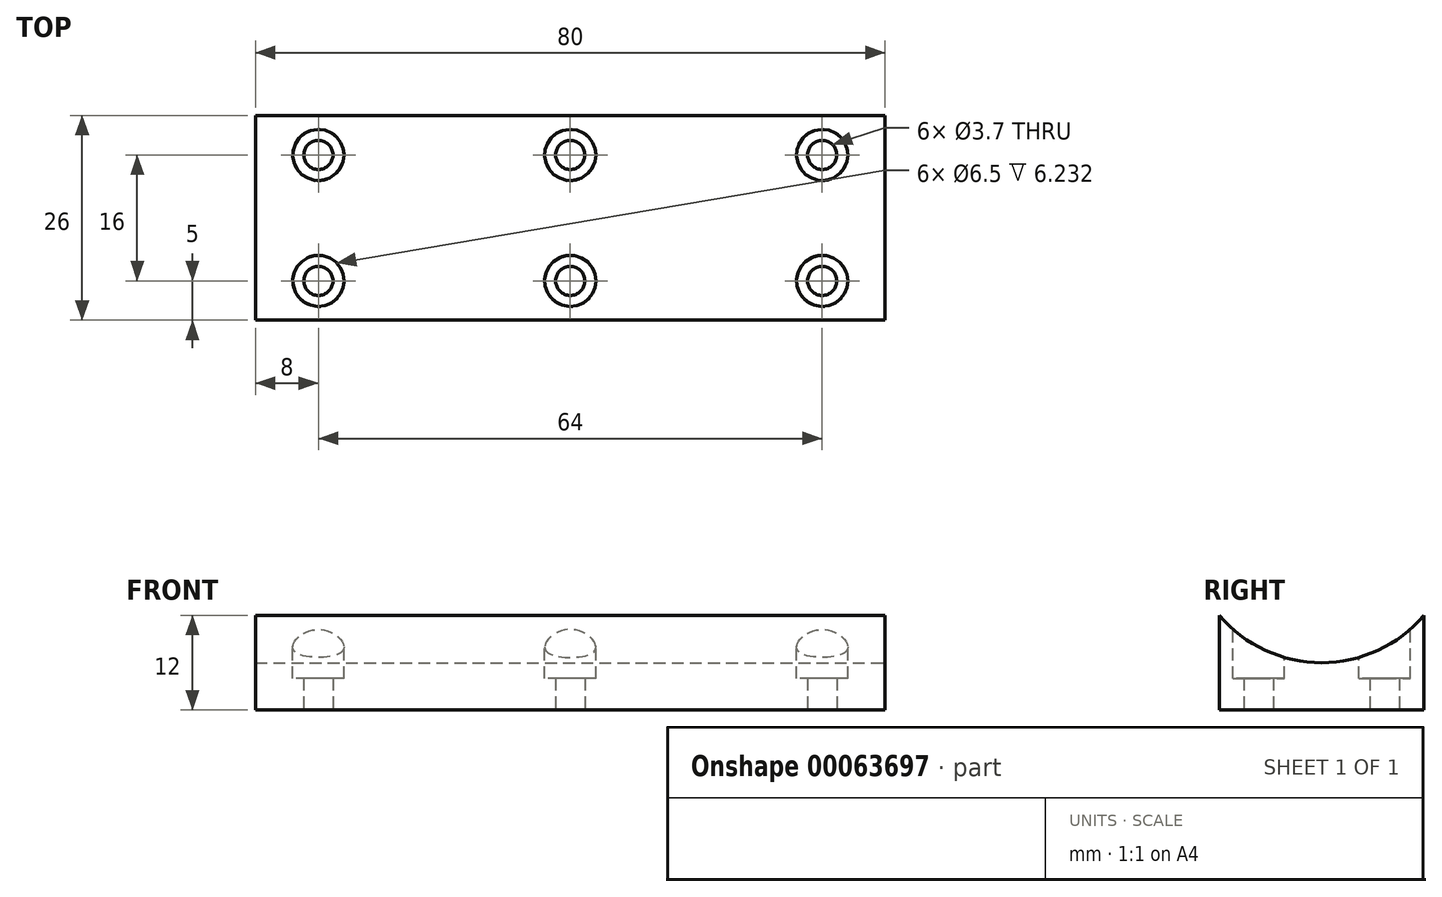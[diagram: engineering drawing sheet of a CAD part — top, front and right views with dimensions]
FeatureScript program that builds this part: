
annotation { "Feature Type Name" : "Feature", "Feature Type Description" : "" }
export const myFeature = defineFeature(function(context is Context, id is Id, definition is map)
    precondition{}
    {
        {
            var Q0;
            Q0=qCreatedBy(makeId("Top.planeOp"),FACE);
            var sketch = newSketch(context, id + "F0", { "sketchPlane" : qUnion([Q0])});
            skLineSegment(sketch, "E0.rect.bottom", {"start": v(-40, -13) * mm, "end": v(40, -13) * mm});
            skLineSegment(sketch, "E0.rect.top", {"start": v(-40, 13) * mm, "end": v(40, 13) * mm});
            skLineSegment(sketch, "E0.rect.left", {"start": v(-40, -13) * mm, "end": v(-40, 13) * mm});
            skLineSegment(sketch, "E0.rect.right", {"start": v(40, -13) * mm, "end": v(40, 13) * mm});
            skPoint(sketch, "E0.rect.middle", {"position": v(0, 0) * mm});
            skCircle(sketch, "E1", {"center": v(0, 8) * mm, "radius": 1.85 * mm});
            skCircle(sketch, "E2.2.0", {"center": v(0, -8) * mm, "radius": 1.85 * mm});
            skPoint(sketch, "E3.1.0.2", {"position": v(32, 0) * mm});
            skCircle(sketch, "E3.1.0.3", {"center": v(32, 8) * mm, "radius": 1.85 * mm});
            skPoint(sketch, "E3.1.0.5", {"position": v(32, 0) * mm});
            skCircle(sketch, "E3.1.0.6", {"center": v(32, -8) * mm, "radius": 1.85 * mm});
            skCircle(sketch, "E4.1.0.0", {"center": v(-32, 8) * mm, "radius": 1.85 * mm});
            skCircle(sketch, "E4.1.0.1", {"center": v(-32, -8) * mm, "radius": 1.85 * mm});
            skLineSegment(sketch, "E4.direction1", {"start": v(0, 8) * mm, "end": v(-32, 8) * mm, "construction": true});
            skSolve(sketch);
        }
        {
            var Q0;
            Q0=makeQuery(id+"F0.imprint","IMPRINT",FACE,{"disambiguationData":[TD([[makeQuery(id+"F0.imprint","IMPRINT",EDGE,{"derivedFrom":sQuery(id+"F0.wireOp",EDGE,"E0.rect.bottom")}),1.0]])]});
            extrude(context, id + "F1", {"entities" : qUnion([Q0]), "depth" : 25 * mm});
        }
        {
            var Q0;
            Q0=makeQuery(id+"F1.opExtrude","SWEPT_FACE",FACE,{"disambiguationData":[OSD([sQuery(id+"F0.wireOp",EDGE,"E0.rect.right")])]});
            var sketch = newSketch(context, id + "F2", { "sketchPlane" : qUnion([Q0])});
            skLineSegment(sketch, "E5", {"start": v(-13, 0) * mm, "end": v(-13, 12) * mm, "construction": true});
            skLineSegment(sketch, "E6", {"start": v(0, 0) * mm, "end": v(0, 6) * mm, "construction": true});
            skPoint(sketch, "E6.endSnap0", {"position": v(0, 0) * mm});
            skArc(sketch, "E7", {"start": v(-13, 12) * mm, "mid": v(0, 6) * mm, "end": v(13, 12) * mm});
            skSolve(sketch);
        }
        {
            var Q0;
            Q0=makeQuery(id+"F1.opExtrude","CAP_FACE",FACE,{"disambiguationData":[OSD([sQuery(id+"F0.wireOp",EDGE,"E0.rect.bottom"),sQuery(id+"F0.wireOp",EDGE,"E0.rect.top"),sQuery(id+"F0.wireOp",EDGE,"E0.rect.left"),sQuery(id+"F0.wireOp",EDGE,"E0.rect.right"),sQuery(id+"F0.wireOp",EDGE,"E1"),sQuery(id+"F0.wireOp",EDGE,"E2.2.0"),sQuery(id+"F0.wireOp",EDGE,"E3.1.0.3"),sQuery(id+"F0.wireOp",EDGE,"E3.1.0.6"),sQuery(id+"F0.wireOp",EDGE,"E4.1.0.0"),sQuery(id+"F0.wireOp",EDGE,"E4.1.0.1")])],"isStart":false});
            var sketch = newSketch(context, id + "F3", { "sketchPlane" : qUnion([Q0])});
            skCircle(sketch, "E8", {"center": v(-32, 8) * mm, "radius": 3.25 * mm});
            skCircle(sketch, "E9", {"center": v(-32, -8) * mm, "radius": 3.25 * mm});
            skCircle(sketch, "E10.1.0.0", {"center": v(0, 8) * mm, "radius": 3.25 * mm});
            skCircle(sketch, "E10.1.0.1", {"center": v(0, -8) * mm, "radius": 3.25 * mm});
            skCircle(sketch, "E10.2.0.0", {"center": v(32, 8) * mm, "radius": 3.25 * mm});
            skCircle(sketch, "E10.2.0.1", {"center": v(32, -8) * mm, "radius": 3.25 * mm});
            skLineSegment(sketch, "E10.direction1", {"start": v(-32, 8) * mm, "end": v(0, 8) * mm, "construction": true});
            skSolve(sketch);
        }
        {
            var Q0;
            Q0=makeQuery(id+"F3.imprint","IMPRINT",FACE,{"disambiguationData":[TD([[makeQuery(id+"F3.imprint","IMPRINT",EDGE,{"derivedFrom":sQuery(id+"F3.wireOp",EDGE,"E9")}),1.0]])]});
            var Q1;
            Q1=makeQuery(id+"F3.imprint","IMPRINT",FACE,{"disambiguationData":[TD([[makeQuery(id+"F3.imprint","IMPRINT",EDGE,{"derivedFrom":sQuery(id+"F3.wireOp",EDGE,"E8")}),1.0]])]});
            var Q2;
            Q2=makeQuery(id+"F3.imprint","IMPRINT",FACE,{"disambiguationData":[TD([[makeQuery(id+"F3.imprint","IMPRINT",EDGE,{"derivedFrom":sQuery(id+"F3.wireOp",EDGE,"E10.1.0.0")}),1.0]])]});
            var Q3;
            Q3=makeQuery(id+"F3.imprint","IMPRINT",FACE,{"disambiguationData":[TD([[makeQuery(id+"F3.imprint","IMPRINT",EDGE,{"derivedFrom":sQuery(id+"F3.wireOp",EDGE,"E10.1.0.1")}),1.0]])]});
            var Q4;
            Q4=makeQuery(id+"F3.imprint","IMPRINT",FACE,{"disambiguationData":[TD([[makeQuery(id+"F3.imprint","IMPRINT",EDGE,{"derivedFrom":sQuery(id+"F3.wireOp",EDGE,"E10.2.0.0")}),1.0]])]});
            var Q5;
            Q5=makeQuery(id+"F3.imprint","IMPRINT",FACE,{"disambiguationData":[TD([[makeQuery(id+"F3.imprint","IMPRINT",EDGE,{"derivedFrom":sQuery(id+"F3.wireOp",EDGE,"E10.2.0.1")}),1.0]])]});
            extrude(context, id + "F4", {"entities" : qUnion([Q0, Q1, Q2, Q3, Q4, Q5]), "operationType" : NewBodyOperationType.REMOVE, "oppositeDirection" : true, "depth" : 21 * mm});
        }
        {
            var Q0;
            {var subQ0=sQuery(id+"F2.wireOp",EDGE,"E7");Q0=makeQuery(id+"F2.imprint","IMPRINT",FACE,{"disambiguationData":[TD([[makeQuery(id+"F2.imprint","IMPRINT",EDGE,{"derivedFrom":subQ0}),1.0]])]});}
            extrude(context, id + "F5", {"entities" : qUnion([Q0]), "operationType" : NewBodyOperationType.REMOVE, "oppositeDirection" : true, "depth" : 100 * mm});
        }
    });
